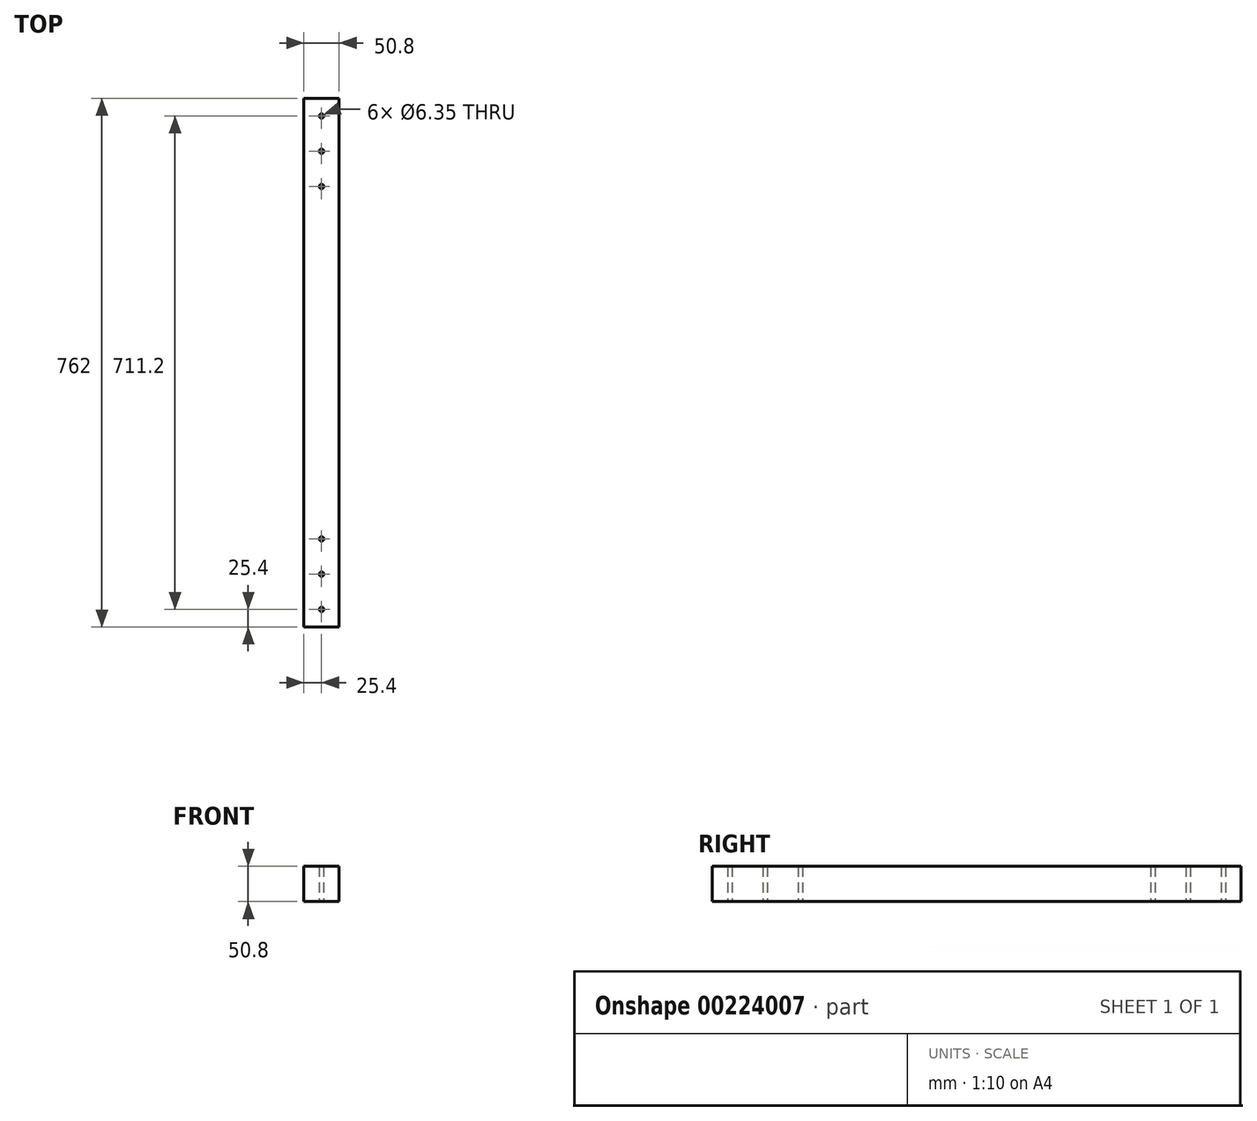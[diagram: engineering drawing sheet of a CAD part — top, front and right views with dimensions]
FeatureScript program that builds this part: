
annotation { "Feature Type Name" : "Feature", "Feature Type Description" : "" }
export const myFeature = defineFeature(function(context is Context, id is Id, definition is map)
    precondition{}
    {
        {
            var Q0;
            Q0=qCreatedBy(makeId("Top.planeOp"),FACE);
            var sketch = newSketch(context, id + "F0", { "sketchPlane" : qUnion([Q0])});
            skLineSegment(sketch, "E0.bottom", {"start": v(0, 0) * mm, "end": v(50.8, 0) * mm});
            skLineSegment(sketch, "E0.top", {"start": v(0, 762) * mm, "end": v(50.8, 762) * mm});
            skLineSegment(sketch, "E0.left", {"start": v(0, 0) * mm, "end": v(0, 762) * mm});
            skLineSegment(sketch, "E0.right", {"start": v(50.8, 0) * mm, "end": v(50.8, 762) * mm});
            skCircle(sketch, "E1", {"center": v(25.4, 25.4) * mm, "radius": 3.18 * mm});
            skCircle(sketch, "E2", {"center": v(25.4, 736.6) * mm, "radius": 3.18 * mm});
            skPoint(sketch, "E2.centerSnap0", {"position": v(25.4, 762) * mm});
            skCircle(sketch, "E3", {"center": v(25.4, 685.8) * mm, "radius": 3.18 * mm});
            skCircle(sketch, "E4", {"center": v(25.4, 635) * mm, "radius": 3.18 * mm});
            skCircle(sketch, "E5", {"center": v(25.4, 127) * mm, "radius": 3.18 * mm});
            skCircle(sketch, "E6", {"center": v(25.4, 76.2) * mm, "radius": 3.18 * mm});
            skSolve(sketch);
        }
        {
            var Q0;
            Q0=makeQuery(id+"F0.imprint","IMPRINT",FACE,{"disambiguationData":[TD([[makeQuery(id+"F0.imprint","IMPRINT",EDGE,{"derivedFrom":sQuery(id+"F0.wireOp",EDGE,"E0.bottom")}),1.0]])]});
            extrude(context, id + "F1", {"entities" : qUnion([Q0]), "depth" : 50.8 * mm});
        }
    });
